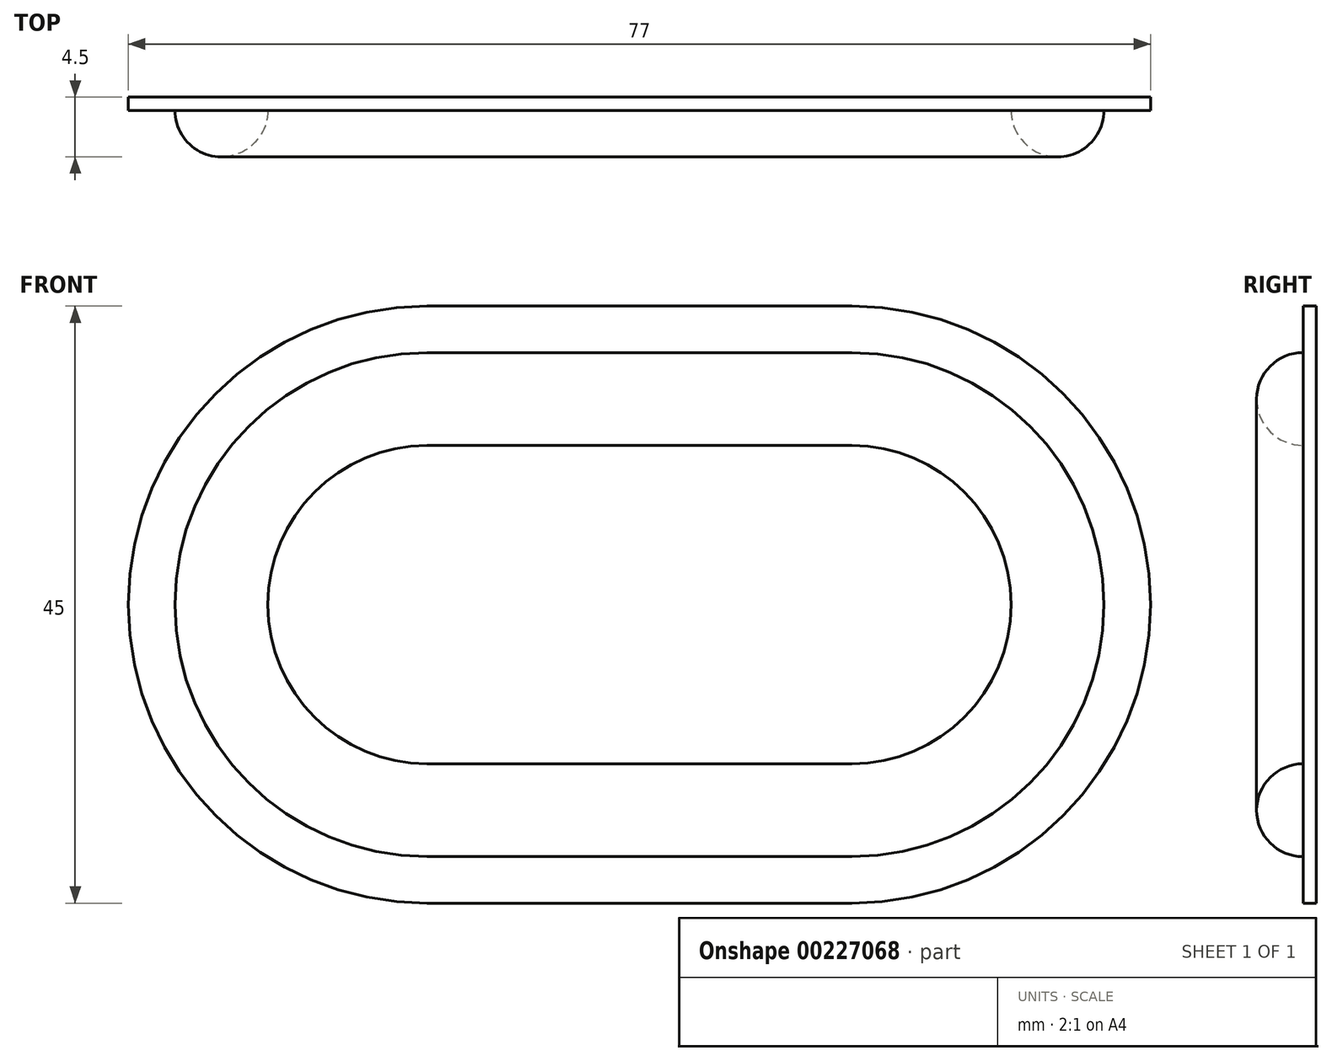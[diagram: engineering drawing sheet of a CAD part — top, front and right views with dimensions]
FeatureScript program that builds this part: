
annotation { "Feature Type Name" : "Feature", "Feature Type Description" : "" }
export const myFeature = defineFeature(function(context is Context, id is Id, definition is map)
    precondition{}
    {
        {
            var Q0;
            Q0=qCreatedBy(makeId("Front.planeOp"),FACE);
            var sketch = newSketch(context, id + "F0", { "sketchPlane" : qUnion([Q0])});
            skLineSegment(sketch, "E0.bottom", {"start": v(16, -22.5) * mm, "end": v(-16, -22.5) * mm});
            skLineSegment(sketch, "E0.top", {"start": v(16, 22.5) * mm, "end": v(-16, 22.5) * mm});
            skLineSegment(sketch, "E0.left", {"start": v(16, -22.5) * mm, "end": v(16, 22.5) * mm});
            skLineSegment(sketch, "E0.right", {"start": v(-16, -22.5) * mm, "end": v(-16, 22.5) * mm});
            skPoint(sketch, "E0.middle", {"position": v(0, 0) * mm});
            skArc(sketch, "E1", {"start": v(-16, 22.5) * mm, "mid": v(-38.5, 0) * mm, "end": v(-16, -22.5) * mm});
            skArc(sketch, "E2", {"start": v(16, -22.5) * mm, "mid": v(38.5, 0) * mm, "end": v(16, 22.5) * mm});
            skSolve(sketch);
        }
        {
            var Q0;
            Q0=makeQuery(id+"F0.imprint","IMPRINT",FACE,{"disambiguationData":[TD([[makeQuery(id+"F0.imprint","IMPRINT",EDGE,{"derivedFrom":sQuery(id+"F0.wireOp",EDGE,"E0.left")}),-1.0]])]});
            var Q1;
            Q1=makeQuery(id+"F0.imprint","IMPRINT",FACE,{"disambiguationData":[TD([[makeQuery(id+"F0.imprint","IMPRINT",EDGE,{"derivedFrom":sQuery(id+"F0.wireOp",EDGE,"E0.bottom")}),-1.0]])]});
            var Q2;
            Q2=makeQuery(id+"F0.imprint","IMPRINT",FACE,{"disambiguationData":[TD([[makeQuery(id+"F0.imprint","IMPRINT",EDGE,{"derivedFrom":sQuery(id+"F0.wireOp",EDGE,"E0.right")}),1.0]])]});
            extrude(context, id + "F1", {"entities" : qUnion([Q0, Q1, Q2]), "depth" : 1 * mm});
        }
        {
            var Q0;
            Q0=makeQuery(id+"F1.opExtrude","CAP_FACE",FACE,{"disambiguationData":[OSD([sQuery(id+"F0.wireOp",EDGE,"E0.bottom"),sQuery(id+"F0.wireOp",EDGE,"E0.top"),sQuery(id+"F0.wireOp",EDGE,"E1"),sQuery(id+"F0.wireOp",EDGE,"E2")])],"isStart":false});
            var sketch = newSketch(context, id + "F2", { "sketchPlane" : qUnion([Q0])});
            skArc(sketch, "E3.0.0", {"start": v(16, -22.5) * mm, "mid": v(38.5, 0) * mm, "end": v(16, 22.5) * mm});
            skLineSegment(sketch, "E3.0.1", {"start": v(16, 22.5) * mm, "end": v(-16, 22.5) * mm});
            skArc(sketch, "E3.0.2", {"start": v(-16, 22.5) * mm, "mid": v(-38.5, 0) * mm, "end": v(-16, -22.5) * mm});
            skLineSegment(sketch, "E3.0.3", {"start": v(-16, -22.5) * mm, "end": v(16, -22.5) * mm});
            skLineSegment(sketch, "E4.0", {"start": v(16, 19) * mm, "end": v(-16, 19) * mm});
            skArc(sketch, "E4.1", {"start": v(16, -19) * mm, "mid": v(35, 0) * mm, "end": v(16, 19) * mm});
            skLineSegment(sketch, "E4.2", {"start": v(-16, -19) * mm, "end": v(16, -19) * mm});
            skArc(sketch, "E4.3", {"start": v(-16, 19) * mm, "mid": v(-35, 0) * mm, "end": v(-16, -19) * mm});
            skArc(sketch, "E5.0", {"start": v(-16, 12) * mm, "mid": v(-28, 0) * mm, "end": v(-16, -12) * mm});
            skLineSegment(sketch, "E5.1", {"start": v(16, 12) * mm, "end": v(-16, 12) * mm});
            skArc(sketch, "E5.2", {"start": v(16, -12) * mm, "mid": v(28, 0) * mm, "end": v(16, 12) * mm});
            skLineSegment(sketch, "E5.3", {"start": v(-16, -12) * mm, "end": v(16, -12) * mm});
            skSolve(sketch);
        }
        {
            var Q0;
            Q0=makeQuery(id+"F2.imprint","IMPRINT",FACE,{"disambiguationData":[TD([[makeQuery(id+"F2.imprint","IMPRINT",EDGE,{"derivedFrom":sQuery(id+"F2.wireOp",EDGE,"E4.0")}),1.0]])]});
            extrude(context, id + "F3", {"entities" : qUnion([Q0]), "operationType" : NewBodyOperationType.ADD, "depth" : 3.5 * mm});
        }
        {
            var Q0;
            Q0=makeQuery(id+"F3.opExtrude","CAP_EDGE",EDGE,{"disambiguationData":[OSD([sQuery(id+"F2.wireOp",EDGE,"E4.0")])],"isStart":false});
            var Q1;
            Q1=makeQuery(id+"F3.opExtrude","CAP_EDGE",EDGE,{"disambiguationData":[OSD([sQuery(id+"F2.wireOp",EDGE,"E5.1")])],"isStart":false});
            fillet(context, id + "F4", {"entities" : qUnion([Q0, Q1]), "radius" : 3.5 * mm, "tangentPropagation" : true, "allowEdgeOverflow" : false});
        }
    });
